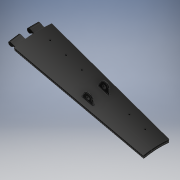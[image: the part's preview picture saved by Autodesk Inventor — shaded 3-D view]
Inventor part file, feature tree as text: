
AUTODESK INVENTOR PART (.ipt)
format: ipt  version: 2019 (Build 230136000, 136)  size: 2,044,928 bytes
history: native  units: mm
features: sketch x9, extrude x5, plane x3, loft x2, shell x2, pattern_circular x2, fillet x1, sweep x1, split x1, other x1
ambient origin geometry x8: Origin, YZ Plane, XZ Plane, XY Plane, X Axis, Y Axis, Z Axis, Center Point
bodies: Solid1 (feature_tree), Solid2 (feature_tree), Solid3 (feature_tree), Solid4 (feature_tree)
feature tree (27):
  sketch  "Sketch1"  dims[d0=291.0mm d1=146.121mm d2=200.0mm]
  plane  "Work Plane1"
  loft  "Loft1"
  shell  "Shell1"  Thickness=200.0mm
  loft  "Loft2"
  shell  "Shell2"  Thickness=2.0mm
  extrude  "Extrusion1"  Depth=195.0mm
  fillet  "Fillet1"  Radius=1.0mm
  pattern_circular  "Circular Pattern1"  [2 undecoded]
  sketch  "Sketch9"  dims[d21=9.0mm]
  extrude  "Extrusion3"  TaperAngle=75.0deg  [1 undecoded]
  pattern_circular  "Circular Pattern2"  Angle=75.0deg  [1 undecoded]
  sweep  "Sweep1"
  sketch  "Sketch8"  dims[d20=15.0mm]
  extrude  "Extrusion2"  Depth=10.0mm
  split  "Split1"
  plane  "Work Plane2"
  plane  "Work Plane3"
  extrude  "Extrusion4"  Depth=10.0mm
  sketch  "Sketch2"  dims[d3=0.0mm d4=90.0deg d5=0.0mm d6=90.0deg d7=2.0mm]
  sketch  "Sketch4"  dims[d9=286.0mm d10=195.0mm]
  sketch  "Sketch5"  dims[d11=0.0mm d12=90.0deg d13=0.0mm d14=90.0deg d15=1.0mm]
  sketch  "Sketch7"  dims[d19=65.0mm]
  sketch  "3D Sketch1"
  other  "Srf1"
  sketch  "Sketch10"  dims[d24=9.0mm d28=4.0mm d29=75.0deg d30=75.0deg d31=1.5mm d32=0.0mm d33=6.5mm d34=7.5mm d35=0.75mm d36=400.0mm d37=360.0deg d39=3.141593mm d40=180.0mm d41=2.0mm d42=0.0mm d44=5.0mm d45=5.5mm d46=1.25mm d47=0.0mm d48=0.0mm d50=13.613568mm d51=1.047198mm d52=2.0mm d53=0.0mm d54=0.5mm d55=0.0mm d56=12.2mm d57=0.0mm d58=400.0mm d59=360.0deg d63=145.0mm d64=20.0mm d65=20.0mm d66=20.0mm d67=60.0mm d68=20.0mm d69=2.0mm d70=3.018547mm d71=10.0mm d72=0.0mm]
  extrude  "ExtrusionSrf1"  Depth=10.0mm
note: 4 required parameter values undecoded (feature->parameter linkage not recoverable at this tier; creation-order binding heuristic only, values carry confidence <= 0.55)
